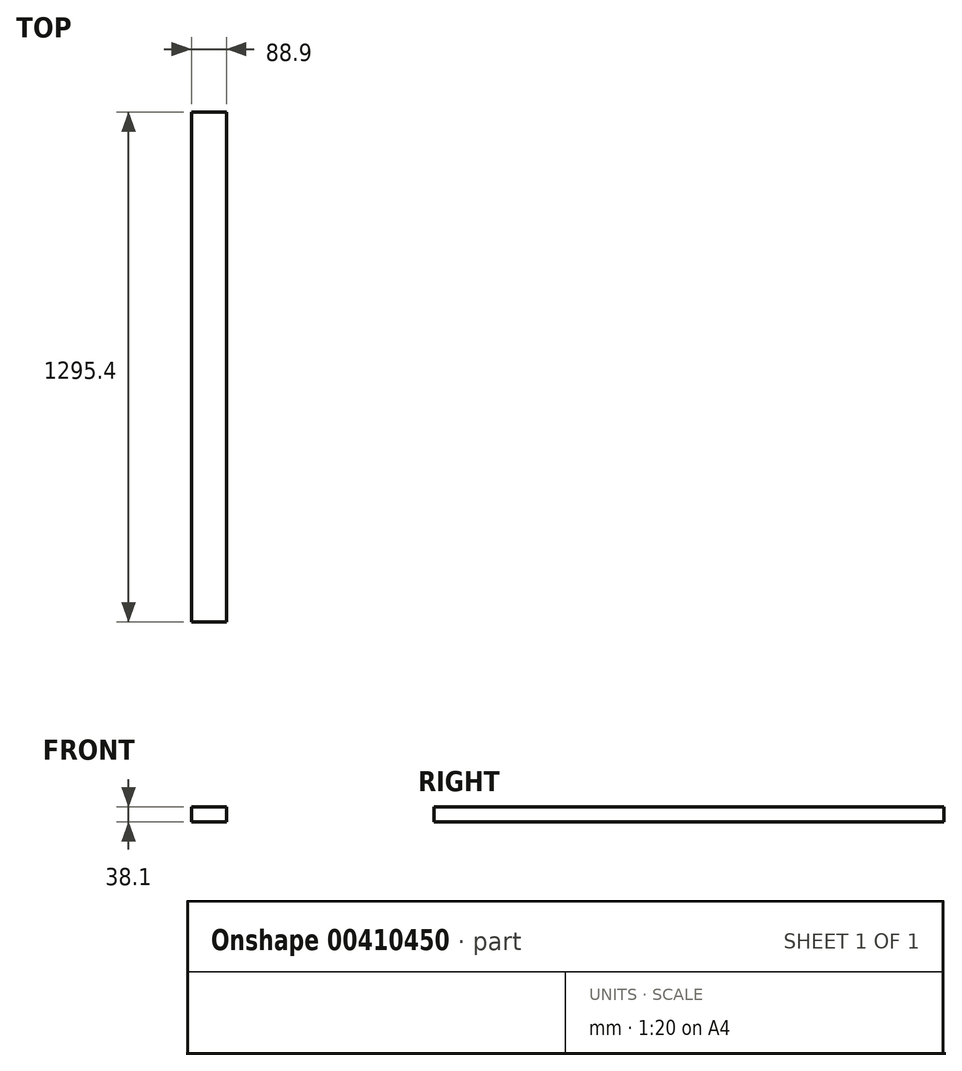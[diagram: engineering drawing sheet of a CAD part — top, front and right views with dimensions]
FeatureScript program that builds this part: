
annotation { "Feature Type Name" : "Feature", "Feature Type Description" : "" }
export const myFeature = defineFeature(function(context is Context, id is Id, definition is map)
    precondition{}
    {
        {
            var Q0;
            Q0=qCreatedBy(makeId("Right.planeOp"),FACE);
            var sketch = newSketch(context, id + "F0", { "sketchPlane" : qUnion([Q0])});
            skLineSegment(sketch, "E0.bottom", {"start": v(-647.7, 19.05) * mm, "end": v(647.7, 19.05) * mm});
            skLineSegment(sketch, "E0.top", {"start": v(-647.7, -19.05) * mm, "end": v(647.7, -19.05) * mm});
            skLineSegment(sketch, "E0.left", {"start": v(-647.7, 19.05) * mm, "end": v(-647.7, -19.05) * mm});
            skLineSegment(sketch, "E0.right", {"start": v(647.7, 19.05) * mm, "end": v(647.7, -19.05) * mm});
            skPoint(sketch, "E0.middle", {"position": v(0, 0) * mm});
            skSolve(sketch);
        }
        {
            var Q0;
            Q0 = qSketchRegion(id + "F0", true);
            extrude(context, id + "F1", {"entities" : qUnion([Q0]), "depth" : 88.9 * mm, "offsetDistance" : 25.4 * mm, "symmetric" : true});
        }
    });
